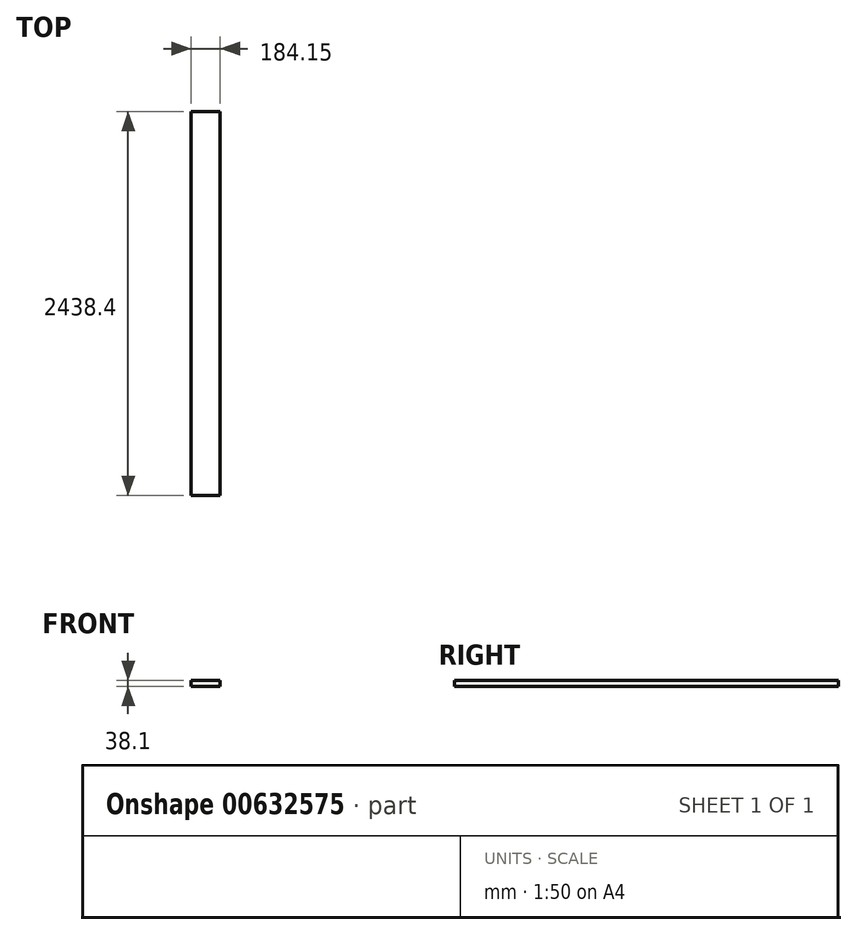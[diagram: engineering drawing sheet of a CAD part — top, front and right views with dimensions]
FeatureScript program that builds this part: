
annotation { "Feature Type Name" : "Feature", "Feature Type Description" : "" }
export const myFeature = defineFeature(function(context is Context, id is Id, definition is map)
    precondition{}
    {
        {
            var Q0;
            Q0=qCreatedBy(makeId("Top.planeOp"),FACE);
            var sketch = newSketch(context, id + "F0", { "sketchPlane" : qUnion([Q0])});
            skLineSegment(sketch, "E0.bottom", {"start": v(-449.6, 1621.06) * mm, "end": v(-265.44, 1621.06) * mm});
            skLineSegment(sketch, "E0.top", {"start": v(-449.6, -817.34) * mm, "end": v(-265.44, -817.34) * mm});
            skLineSegment(sketch, "E0.left", {"start": v(-449.6, 1621.06) * mm, "end": v(-449.6, -817.34) * mm});
            skLineSegment(sketch, "E0.right", {"start": v(-265.44, 1621.06) * mm, "end": v(-265.44, -817.34) * mm});
            skSolve(sketch);
        }
        {
            var Q0;
            Q0 = qSketchRegion(id + "F0", true);
            extrude(context, id + "F1", {"entities" : qUnion([Q0]), "depth" : 38.1 * mm, "offsetDistance" : 25.4 * mm});
        }
    });
